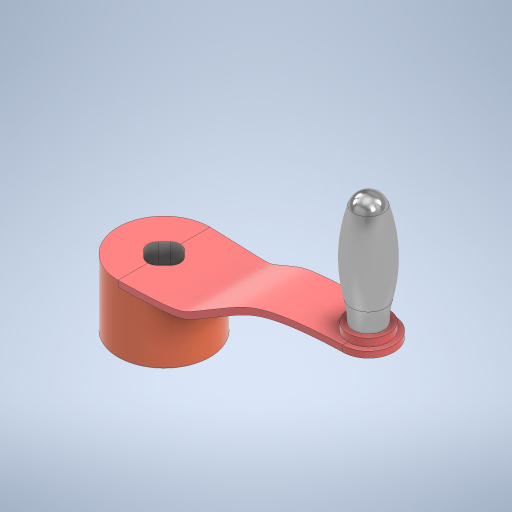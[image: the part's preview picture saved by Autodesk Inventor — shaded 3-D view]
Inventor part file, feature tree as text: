
AUTODESK INVENTOR PART (.ipt)
format: ipt  version: 2024 (Build 280153000, 153)  size: 467,968 bytes
history: native  units: mm
features: sketch x8, extrude x6, plane x4, other x3, fillet x2, loft x1, revolve x1
ambient origin geometry x8: Origin, YZ Plane, XZ Plane, XY Plane, X Axis, Y Axis, Z Axis, Center Point
bodies: Body1 (feature_tree)
feature tree (25):
  sketch  "Skizze1"  dims[d2=45.0mm d11=200.0mm]
  sketch  "Skizze2"  dims[d12=60.0mm d13=50.0mm]
  plane  "Arbeitsebene1"
  plane  "Arbeitsebene2"
  sketch  "Skizze4"  dims[d14=35.0mm d15=200.0mm d16=35.0mm]
  extrude  "Extrusion3"  Depth=200.0mm
  extrude  "Extrusion4"  Depth=50.0mm
  loft  "Erhebung1"
  extrude  "Extrusion5"  Depth=37.0mm
  extrude  "Extrusion6"  Depth=6.0mm TaperAngle=0.0deg
  plane  "Arbeitsebene3"
  extrude  "Extrusion12"  TaperAngle=0.0deg  [1 undecoded]
  extrude  "Extrusion13"  Depth=30.0mm
  other  "Arbeitsachse2"
  plane  "Arbeitsebene4"
  revolve  "Umdrehung1"
  fillet  "Rundung1"  Radius=40.0mm
  fillet  "Rundung2"  Radius=7.5mm
  other  "Kanten1"
  other  "Kanten2"
  sketch  "Skizze8"  dims[d17=25.0mm d18=37.0mm]
  sketch  "Skizze10"  dims[d23=6.0mm d24=0.0mm d25=6.0mm d26=0.0mm]
  sketch  "Skizze12"  dims[d27=0.0mm d28=90.0deg d29=0.0mm d30=90.0deg]
  sketch  "Skizze13"  dims[d31=0.0mm d32=90.0deg d33=30.0mm d34=40.0mm d35=7.5mm d36=0.0mm]
  sketch  "Skizze14"  dims[d39=60.0mm d40=0.0mm d52=-25.0mm d53=40.0mm d54=0.0mm d55=0.0mm d56=10.0mm d57=0.0mm d58=200.0mm d61=150.0mm d62=75.0mm d63=109.5mm d65=90.0deg d66=20.0mm d68=15.0mm d69=0.9mm d70=10.0mm d71=90.0mm d59=0.75mm d60=20.594885mm]
note: 1 required parameter value undecoded (feature->parameter linkage not recoverable at this tier; creation-order binding heuristic only, values carry confidence <= 0.55)
